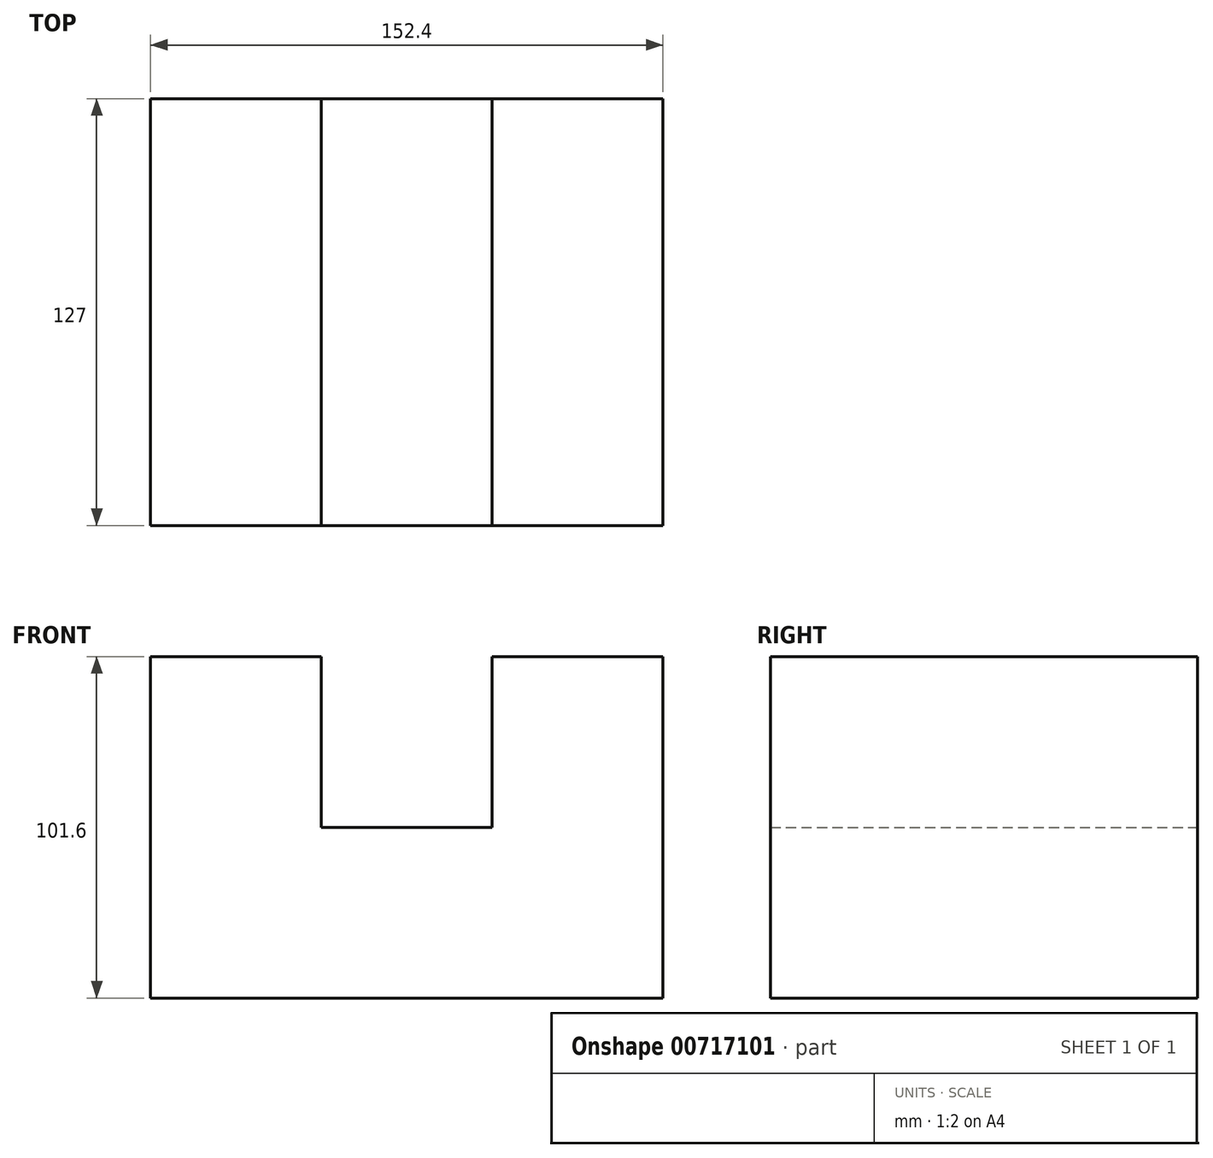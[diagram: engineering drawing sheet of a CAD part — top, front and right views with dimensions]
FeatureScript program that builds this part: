
annotation { "Feature Type Name" : "Feature", "Feature Type Description" : "" }
export const myFeature = defineFeature(function(context is Context, id is Id, definition is map)
    precondition{}
    {
        {
            var Q0;
            Q0=qCreatedBy(makeId("Front.planeOp"),FACE);
            var sketch = newSketch(context, id + "F0", { "sketchPlane" : qUnion([Q0])});
            skLineSegment(sketch, "E0", {"start": v(-62.05, -66.14) * mm, "end": v(90.35, -66.14) * mm});
            skLineSegment(sketch, "E1", {"start": v(90.35, -66.14) * mm, "end": v(90.35, 35.46) * mm});
            skLineSegment(sketch, "E2", {"start": v(90.35, 35.46) * mm, "end": v(39.55, 35.46) * mm});
            skLineSegment(sketch, "E3", {"start": v(39.55, 35.46) * mm, "end": v(39.55, -15.34) * mm});
            skLineSegment(sketch, "E4", {"start": v(39.55, -15.34) * mm, "end": v(-11.25, -15.34) * mm});
            skLineSegment(sketch, "E5", {"start": v(-11.25, -15.34) * mm, "end": v(-11.25, 35.46) * mm});
            skLineSegment(sketch, "E6", {"start": v(-11.25, 35.46) * mm, "end": v(-62.05, 35.46) * mm});
            skLineSegment(sketch, "E7", {"start": v(-62.05, 35.46) * mm, "end": v(-62.05, -66.14) * mm});
            skSolve(sketch);
        }
        {
            var Q0;
            Q0 = qSketchRegion(id + "F0", true);
            extrude(context, id + "F1", {"entities" : qUnion([Q0]), "depth" : 127 * mm, "offsetDistance" : 25.4 * mm});
        }
    });
